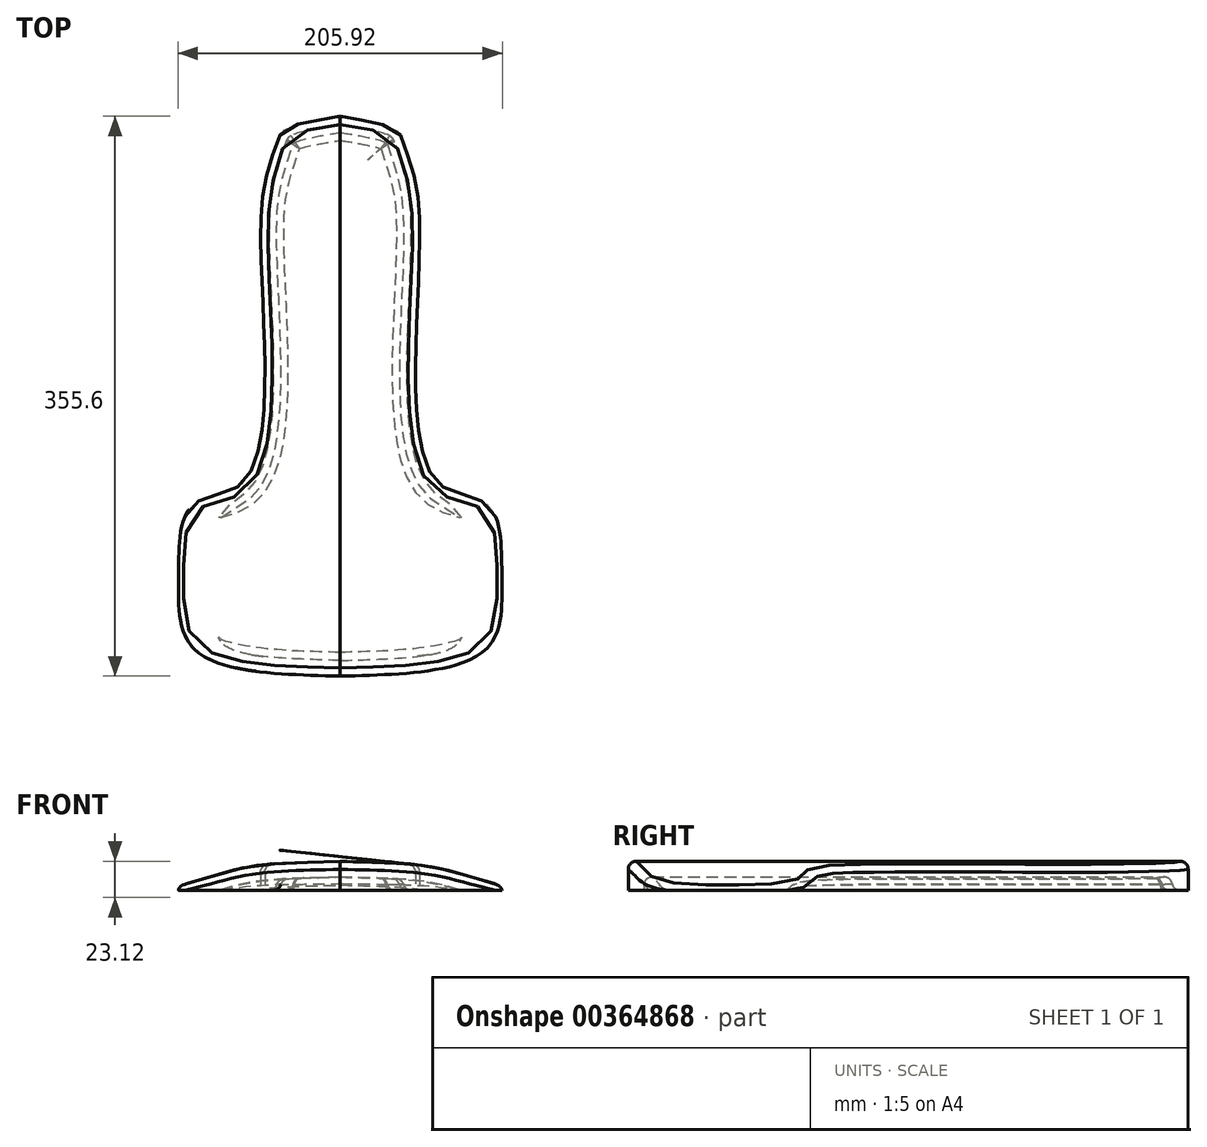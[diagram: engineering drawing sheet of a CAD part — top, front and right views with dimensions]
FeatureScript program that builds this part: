
annotation { "Feature Type Name" : "Feature", "Feature Type Description" : "" }
export const myFeature = defineFeature(function(context is Context, id is Id, definition is map)
    precondition{}
    {
        {
            var Q0;
            Q0=qCreatedBy(makeId("Front.planeOp"),FACE);
            var sketch = newSketch(context, id + "F0", { "sketchPlane" : qUnion([Q0])});
            skFitSpline(sketch, "E0", {"points": [v(-106.6, 0) * mm, v(-100.36, 3.2) * mm, v(-86.34, 7.47) * mm, v(-61.87, 14.17) * mm, v(-28.35, 17.53) * mm, v(0, 18.44) * mm], "startDerivative": vector(46.64, 27.05) * mm, "endDerivative": vector(86.6, 4.11) * mm});
            skFitSpline(sketch, "E1.MirrorCS", {"points": [v(106.6, 0) * mm, v(100.36, 3.2) * mm, v(86.34, 7.47) * mm, v(61.87, 14.17) * mm, v(28.35, 17.53) * mm, v(0, 18.44) * mm], "startDerivative": vector(-46.64, 27.05) * mm, "endDerivative": vector(-86.6, 4.11) * mm});
            skLineSegment(sketch, "E2", {"start": v(-106.6, 0) * mm, "end": v(106.6, 0) * mm});
            skSolve(sketch);
        }
        {
            var Q0;
            Q0=makeQuery(id+"F0.imprint","IMPRINT",FACE,{"disambiguationData":[TD([[makeQuery(id+"F0.imprint","IMPRINT",EDGE,{"derivedFrom":sQuery(id+"F0.wireOp",EDGE,"E0")}),-1.0]])]});
            extrude(context, id + "F1", {"entities" : qUnion([Q0]), "endBound" : BoundingType.SYMMETRIC, "depth" : 355.6 * mm});
        }
        {
            var Q0;
            Q0=makeQuery(id+"F1.opExtrude","SWEPT_FACE",FACE,{"disambiguationData":[OSD([sQuery(id+"F0.wireOp",EDGE,"E2")])]});
            var sketch = newSketch(context, id + "F2", { "sketchPlane" : qUnion([Q0])});
            skFitSpline(sketch, "E3", {"points": [v(0, -177.8) * mm, v(20.2, -174.26) * mm, v(36.23, -168.38) * mm, v(41.3, -157.96) * mm, v(48.52, -132.05) * mm, v(49.85, -76.74) * mm, v(49.18, 16.9) * mm, v(63.67, 56.48) * mm, v(84.9, 64.2) * mm, v(98.42, 75.8) * mm, v(102.88, 115.54) * mm, v(92.7, 160.58) * mm, v(0, 177.8) * mm], "startDerivative": vector(321.72, 51.47) * mm, "endDerivative": vector(-866.46, 22.75) * mm});
            skFitSpline(sketch, "E4.MirrorCS", {"points": [v(0, -177.8) * mm, v(-20.2, -174.26) * mm, v(-36.23, -168.38) * mm, v(-41.3, -157.96) * mm, v(-48.52, -132.05) * mm, v(-49.85, -76.74) * mm, v(-49.18, 16.9) * mm, v(-63.67, 56.48) * mm, v(-84.9, 64.2) * mm, v(-98.42, 75.8) * mm, v(-102.88, 115.54) * mm, v(-92.7, 160.58) * mm, v(0, 177.8) * mm], "startDerivative": vector(-321.72, 51.47) * mm, "endDerivative": vector(866.46, 22.75) * mm});
            skSolve(sketch);
        }
        {
            var Q0;
            {var subQ0=sQuery(id+"F2.wireOp",EDGE,"E3");Q0=makeQuery(id+"F2.imprint","IMPRINT",FACE,{"disambiguationData":[TD([[makeQuery(id+"F2.imprint","IMPRINT",EDGE,{"derivedFrom":subQ0}),-1.0]])]});}
            var Q1;
            {var subQ0=sQuery(id+"F2.wireOp",EDGE,"E4.MirrorCS");Q1=makeQuery(id+"F2.imprint","IMPRINT",FACE,{"disambiguationData":[TD([[makeQuery(id+"F2.imprint","IMPRINT",EDGE,{"derivedFrom":subQ0}),1.0]])]});}
            extrude(context, id + "F3", {"entities" : qUnion([Q0, Q1]), "operationType" : NewBodyOperationType.REMOVE, "oppositeDirection" : true, "depth" : 50.8 * mm});
        }
        {
            var Q0;
            Q0=makeQuery(id+"F3.boolean.opBoolean","INTERSECT",EDGE,{"derivedFrom":[makeQuery(id+"F1.opExtrude","SWEPT_FACE",FACE,{"disambiguationData":[OSD([sQuery(id+"F0.wireOp",EDGE,"E1.MirrorCS")])]}),makeQuery(id+"F3.opExtrude","SWEPT_FACE",FACE,{"disambiguationData":[OSD([sQuery(id+"F2.wireOp",EDGE,"E3")])]})]});
            var Q1;
            Q1=makeQuery(id+"F3.boolean.opBoolean","INTERSECT",EDGE,{"derivedFrom":[makeQuery(id+"F1.opExtrude","SWEPT_FACE",FACE,{"disambiguationData":[OSD([sQuery(id+"F0.wireOp",EDGE,"E0")])]}),makeQuery(id+"F3.opExtrude","SWEPT_FACE",FACE,{"disambiguationData":[OSD([sQuery(id+"F2.wireOp",EDGE,"E4.MirrorCS")])]})]});
            fillet(context, id + "F4", {"entities" : qUnion([Q0, Q1]), "radius" : 5.08 * mm, "tangentPropagation" : true, "allowEdgeOverflow" : false});
        }
        {
            var Q0;
            Q0=makeQuery(id+"F1.opExtrude","SWEPT_FACE",FACE,{"disambiguationData":[OSD([sQuery(id+"F0.wireOp",EDGE,"E2")])]});
            shell(context, id + "F5", {"entities" : qUnion([Q0]), "thickness" : 10 * mm});
        }
        {
            var Q0;
            {var subQ0=sQuery(id+"F2.wireOp",EDGE,"E4.MirrorCS");var subQ1=makeQuery(id+"F3.opExtrude","SWEPT_FACE",FACE,{"disambiguationData":[OSD([subQ0])]});var subQ2=sQuery(id+"F0.wireOp",EDGE,"E0");var subQ3=makeQuery(id+"F1.opExtrude","SWEPT_FACE",FACE,{"disambiguationData":[OSD([subQ2])]});var subQ4=makeQuery(id+"F3.boolean.opBoolean","INTERSECT",EDGE,{"derivedFrom":[subQ3,subQ1]});Q0=makeQuery(id+"F5.opShell","OFFSET_EDGE",EDGE,{"disambiguationData":[OSD([subQ2,subQ0]),TDD([makeQuery(id+"F4.opFillet","BLEND_EDGE",EDGE,{"blendedFrom":[subQ4,subQ3],"blendedInto":[subQ3]}),makeQuery(id+"F4.opFillet","BLEND_EDGE",EDGE,{"disambiguationData":[OD(0.0)],"blendedFrom":[subQ4,makeQuery(id+"F3.boolean.opBoolean","COPY",FACE,{"derivedFrom":subQ1})],"blendedInto":[makeQuery(id+"F3.boolean.opBoolean","COPY",FACE,{"derivedFrom":subQ1})]})])]});}
            var Q1;
            {var subQ0=sQuery(id+"F2.wireOp",EDGE,"E3");var subQ1=makeQuery(id+"F3.opExtrude","SWEPT_FACE",FACE,{"disambiguationData":[OSD([subQ0])]});var subQ2=sQuery(id+"F0.wireOp",EDGE,"E1.MirrorCS");var subQ3=makeQuery(id+"F1.opExtrude","SWEPT_FACE",FACE,{"disambiguationData":[OSD([subQ2])]});var subQ4=makeQuery(id+"F3.boolean.opBoolean","INTERSECT",EDGE,{"derivedFrom":[subQ3,subQ1]});Q1=makeQuery(id+"F5.opShell","OFFSET_EDGE",EDGE,{"disambiguationData":[OSD([subQ2,subQ0]),TDD([makeQuery(id+"F4.opFillet","BLEND_EDGE",EDGE,{"blendedFrom":[subQ4,subQ3],"blendedInto":[subQ3]}),makeQuery(id+"F4.opFillet","BLEND_EDGE",EDGE,{"disambiguationData":[OD(0.0)],"blendedFrom":[subQ4,makeQuery(id+"F3.boolean.opBoolean","COPY",FACE,{"derivedFrom":subQ1})],"blendedInto":[makeQuery(id+"F3.boolean.opBoolean","COPY",FACE,{"derivedFrom":subQ1})]})])]});}
            fillet(context, id + "F6", {"entities" : qUnion([Q0, Q1]), "radius" : 5.08 * mm, "tangentPropagation" : true, "allowEdgeOverflow" : false});
        }
        {
            var Q0;
            {var subQ0=makeQuery(id+"F1.opExtrude","SWEPT_FACE",FACE,{"disambiguationData":[OSD([sQuery(id+"F0.wireOp",EDGE,"E2")])]});var subQ1=makeQuery(id+"F3.opExtrude","SWEPT_FACE",FACE,{"disambiguationData":[OSD([sQuery(id+"F2.wireOp",EDGE,"E3")])]});var subQ2=makeQuery(id+"F3.boolean.opBoolean","COPY",FACE,{"derivedFrom":subQ1});var subQ3=makeQuery(id+"F3.boolean.opBoolean","INTERSECT",EDGE,{"derivedFrom":[makeQuery(id+"F1.opExtrude","SWEPT_FACE",FACE,{"disambiguationData":[OSD([sQuery(id+"F0.wireOp",EDGE,"E1.MirrorCS")])]}),subQ1]});Q0=makeQuery(id+"F5.opShell","SHELL_CAP_EDGE",EDGE,{"derivedFrom":[makeQuery(id+"F4.opFillet","BLEND_VERTEX",VERTEX,{"disambiguationData":[OD(0.0)],"blendedFrom":[subQ3,subQ2,subQ0],"blendedInto":[subQ2,subQ0]}),makeQuery(id+"F4.opFillet","BLEND_VERTEX",VERTEX,{"disambiguationData":[OD(1.0)],"blendedFrom":[subQ3,subQ2,subQ0],"blendedInto":[subQ2,subQ0]})]});}
            var Q1;
            {var subQ0=makeQuery(id+"F1.opExtrude","SWEPT_FACE",FACE,{"disambiguationData":[OSD([sQuery(id+"F0.wireOp",EDGE,"E2")])]});var subQ1=makeQuery(id+"F3.opExtrude","SWEPT_FACE",FACE,{"disambiguationData":[OSD([sQuery(id+"F2.wireOp",EDGE,"E4.MirrorCS")])]});var subQ2=makeQuery(id+"F3.boolean.opBoolean","COPY",FACE,{"derivedFrom":subQ1});var subQ3=makeQuery(id+"F3.boolean.opBoolean","INTERSECT",EDGE,{"derivedFrom":[makeQuery(id+"F1.opExtrude","SWEPT_FACE",FACE,{"disambiguationData":[OSD([sQuery(id+"F0.wireOp",EDGE,"E0")])]}),subQ1]});Q1=makeQuery(id+"F5.opShell","SHELL_CAP_EDGE",EDGE,{"derivedFrom":[makeQuery(id+"F4.opFillet","BLEND_VERTEX",VERTEX,{"disambiguationData":[OD(0.0)],"blendedFrom":[subQ3,subQ2,subQ0],"blendedInto":[subQ2,subQ0]}),makeQuery(id+"F4.opFillet","BLEND_VERTEX",VERTEX,{"disambiguationData":[OD(1.0)],"blendedFrom":[subQ3,subQ2,subQ0],"blendedInto":[subQ2,subQ0]})]});}
            fillet(context, id + "F7", {"entities" : qUnion([Q0, Q1]), "radius" : 5.08 * mm, "tangentPropagation" : true, "allowEdgeOverflow" : false});
        }
        {
            var Q0;
            {var subQ0=sQuery(id+"F2.wireOp",EDGE,"E4.MirrorCS");var subQ1=makeQuery(id+"F3.opExtrude","SWEPT_FACE",FACE,{"disambiguationData":[OSD([subQ0])]});var subQ2=sQuery(id+"F0.wireOp",EDGE,"E0");var subQ3=makeQuery(id+"F1.opExtrude","SWEPT_FACE",FACE,{"disambiguationData":[OSD([subQ2])]});var subQ4=makeQuery(id+"F3.boolean.opBoolean","INTERSECT",EDGE,{"derivedFrom":[subQ3,subQ1]});Q0=makeQuery(id+"F5.opShell","OFFSET_EDGE",EDGE,{"disambiguationData":[OSD([subQ2,subQ0]),TDD([makeQuery(id+"F4.opFillet","BLEND_EDGE",EDGE,{"blendedFrom":[subQ4,subQ3],"blendedInto":[subQ3]}),makeQuery(id+"F4.opFillet","BLEND_EDGE",EDGE,{"disambiguationData":[OD(1.0)],"blendedFrom":[subQ4,makeQuery(id+"F3.boolean.opBoolean","COPY",FACE,{"derivedFrom":subQ1})],"blendedInto":[makeQuery(id+"F3.boolean.opBoolean","COPY",FACE,{"derivedFrom":subQ1})]})])]});}
            var Q1;
            {var subQ0=sQuery(id+"F2.wireOp",EDGE,"E3");var subQ1=makeQuery(id+"F3.opExtrude","SWEPT_FACE",FACE,{"disambiguationData":[OSD([subQ0])]});var subQ2=sQuery(id+"F0.wireOp",EDGE,"E1.MirrorCS");var subQ3=makeQuery(id+"F1.opExtrude","SWEPT_FACE",FACE,{"disambiguationData":[OSD([subQ2])]});var subQ4=makeQuery(id+"F3.boolean.opBoolean","INTERSECT",EDGE,{"derivedFrom":[subQ3,subQ1]});Q1=makeQuery(id+"F5.opShell","OFFSET_EDGE",EDGE,{"disambiguationData":[OSD([subQ2,subQ0]),TDD([makeQuery(id+"F4.opFillet","BLEND_EDGE",EDGE,{"blendedFrom":[subQ4,subQ3],"blendedInto":[subQ3]}),makeQuery(id+"F4.opFillet","BLEND_EDGE",EDGE,{"disambiguationData":[OD(1.0)],"blendedFrom":[subQ4,makeQuery(id+"F3.boolean.opBoolean","COPY",FACE,{"derivedFrom":subQ1})],"blendedInto":[makeQuery(id+"F3.boolean.opBoolean","COPY",FACE,{"derivedFrom":subQ1})]})])]});}
            fillet(context, id + "F8", {"entities" : qUnion([Q0, Q1]), "radius" : 5.08 * mm, "tangentPropagation" : true, "allowEdgeOverflow" : false});
        }
    });
